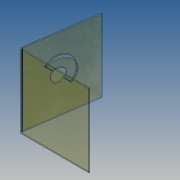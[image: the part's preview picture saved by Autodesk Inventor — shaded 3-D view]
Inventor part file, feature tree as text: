
AUTODESK INVENTOR PART (.ipt)
format: ipt  version: 2017 (Build 210142000, 142)  size: 191,488 bytes
history: native  units: mm
features: other x4, sketch x3, extrude x3, thicken_offset x1, sheet_metal_op x1, reference x1
ambient origin geometry x8: Origin, YZ Plane, XZ Plane, XY Plane, X Axis, Y Axis, Z Axis, Center Point
bodies: Solid1 (feature_tree)
feature tree (13):
  thicken_offset  "Thicken1"
  sketch  "Sketch2"  dims[d2=48.0mm d3=45.0mm]
  extrude  "Extrusion1"  Depth=49.0mm
  sheet_metal_op  "Fold1"
  extrude  "Extrusion2"  Depth=45.0mm
  sketch  "Sketch1"  dims[d0=49.0mm d1=49.0mm]
  reference  "Reference1"
  other  "Srf1"
  sketch  "Sketch3"  dims[d4=6.0mm d5=3.0mm d6=98.0mm d7=0.0mm d8=1.5mm d9=1.0mm d10=315.0deg d11=21.0mm d12=8.0mm d13=98.0mm d14=0.0mm d15=1.5mm d16=0.75mm d17=3.0mm d18=1.5mm d19=2.792527mm d20=1.5mm d21=18.0mm d22=98.0mm d23=0.0mm]
  extrude  "ExtrusionSrf1"  Depth=3.0mm
  other  "<userpath>\Dropbox\multiactuador\case.iam"
  other  "case.iam"
  other  "remache:3"
